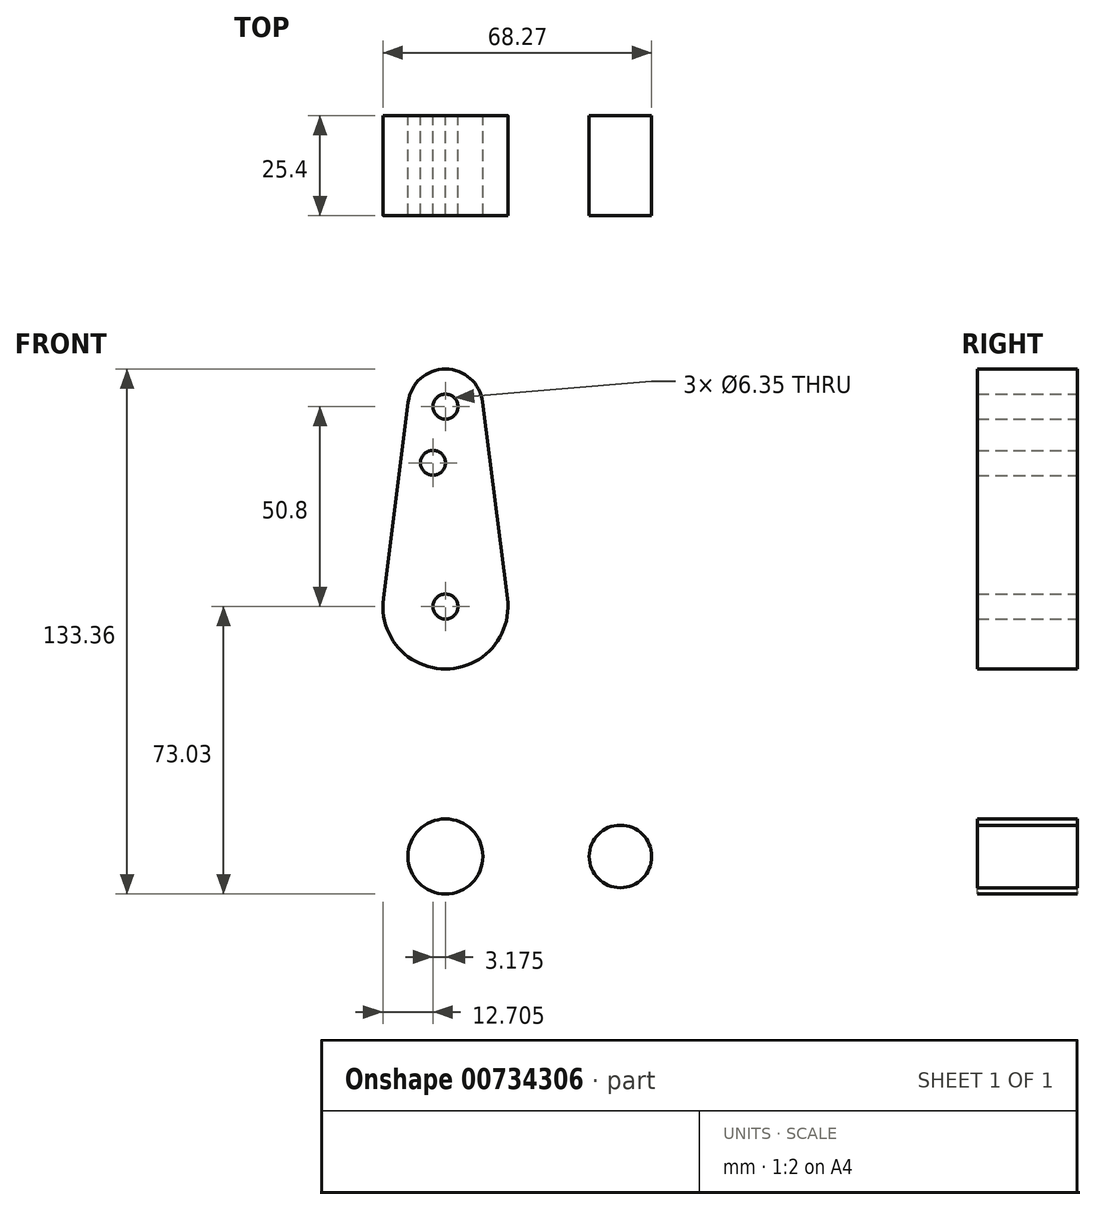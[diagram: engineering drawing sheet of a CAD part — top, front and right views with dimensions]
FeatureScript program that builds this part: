
annotation { "Feature Type Name" : "Feature", "Feature Type Description" : "" }
export const myFeature = defineFeature(function(context is Context, id is Id, definition is map)
    precondition{}
    {
        {
            var Q0;
            Q0=qCreatedBy(makeId("Front.planeOp"),FACE);
            var sketch = newSketch(context, id + "F0", { "sketchPlane" : qUnion([Q0])});
            skLineSegment(sketch, "E0", {"start": v(0, 0) * mm, "end": v(0, 114.3) * mm, "construction": true});
            skLineSegment(sketch, "E1", {"start": v(0, 0) * mm, "end": v(44.45, 0) * mm, "construction": true});
            skCircle(sketch, "E2", {"center": v(0, 114.3) * mm, "radius": 9.53 * mm});
            skCircle(sketch, "E3", {"center": v(0, 63.5) * mm, "radius": 15.88 * mm});
            skCircle(sketch, "E4", {"center": v(0, 0) * mm, "radius": 9.53 * mm});
            skCircle(sketch, "E5", {"center": v(44.45, 0) * mm, "radius": 7.94 * mm});
            skLineSegment(sketch, "E6", {"start": v(18.97, 8.85) * mm, "end": v(44.73, 7.93) * mm});
            skLineSegment(sketch, "E7", {"start": v(0, -9.53) * mm, "end": v(44.73, -7.93) * mm});
            skLineSegment(sketch, "E8", {"start": v(-15.75, 65.48) * mm, "end": v(-9.45, 115.5) * mm});
            skLineSegment(sketch, "E9", {"start": v(9.45, 115.5) * mm, "end": v(15.75, 65.48) * mm});
            skLineSegment(sketch, "E10", {"start": v(15.8, 61.91) * mm, "end": v(11.34, 17.59) * mm});
            skLineSegment(sketch, "E11", {"start": v(-15.8, 61.91) * mm, "end": v(-9.52, 0) * mm});
            skCircle(sketch, "E12", {"center": v(0, 114.3) * mm, "radius": 3.18 * mm});
            skCircle(sketch, "E13", {"center": v(0, 63.5) * mm, "radius": 3.18 * mm});
            skCircle(sketch, "E14", {"center": v(0, 0) * mm, "radius": 3.18 * mm});
            skCircle(sketch, "E15", {"center": v(44.45, 0) * mm, "radius": 3.18 * mm});
            skCircle(sketch, "E16", {"center": v(-3.18, 100.03) * mm, "radius": 3.18 * mm});
            skArc(sketch, "E17.filletArc", {"start": v(11.34, 17.59) * mm, "mid": v(13.26, 11.57) * mm, "end": v(18.97, 8.85) * mm});
            skSolve(sketch);
        }
        {
            var Q0;
            Q0 = qSketchRegion(id + "F0", true);
            extrude(context, id + "F1", {"entities" : qUnion([Q0]), "depth" : 25.4 * mm, "offsetDistance" : 25.4 * mm});
        }
    });
